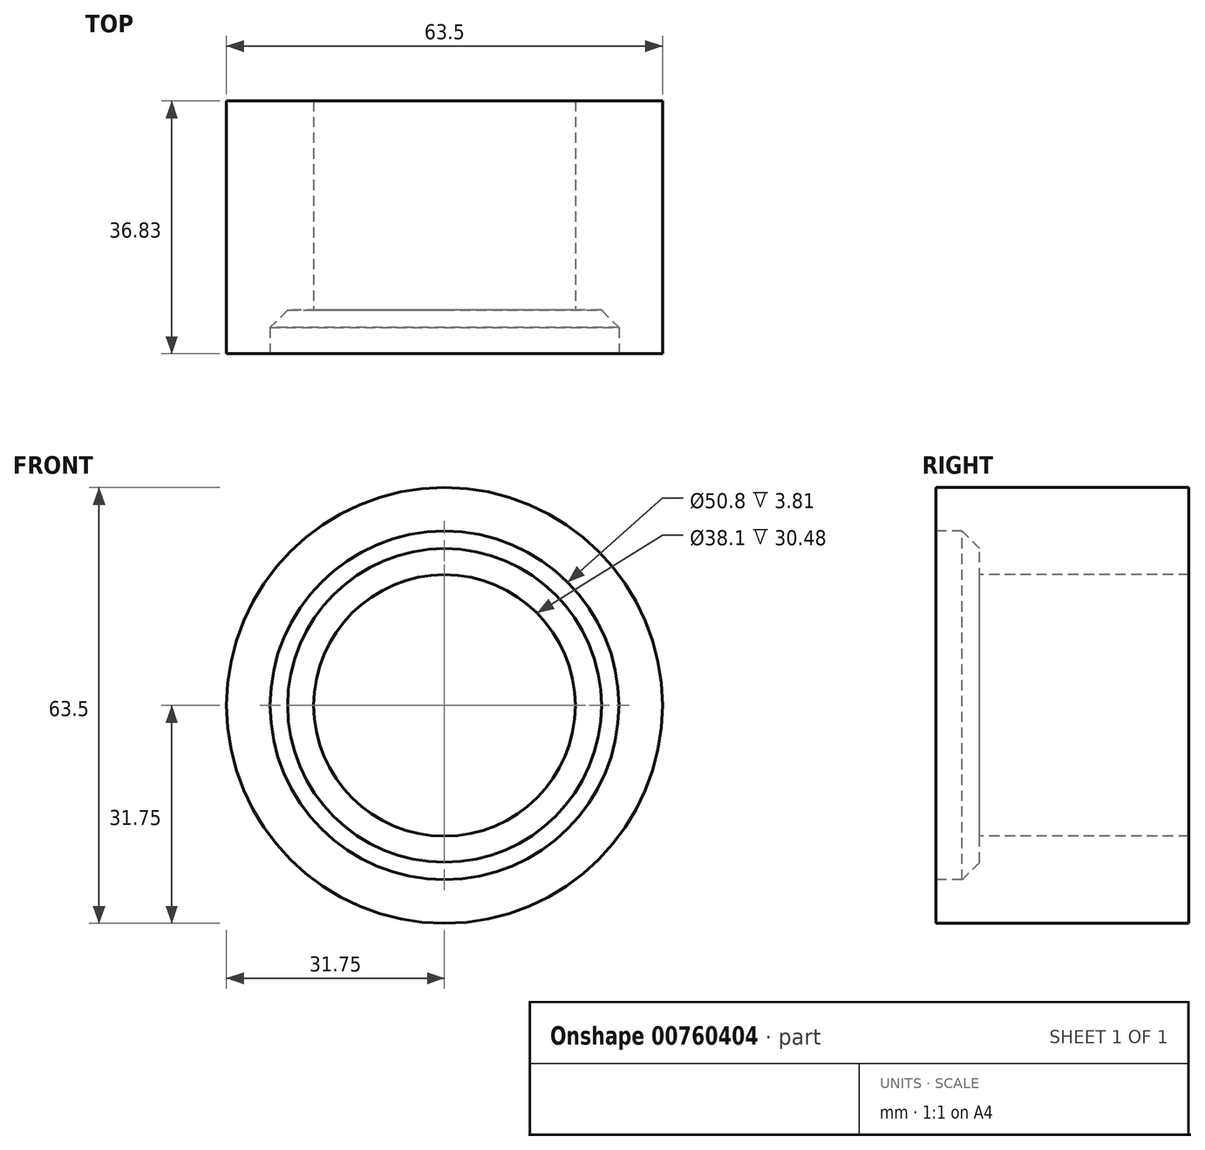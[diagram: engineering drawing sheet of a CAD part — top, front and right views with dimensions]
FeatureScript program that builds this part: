
annotation { "Feature Type Name" : "Feature", "Feature Type Description" : "" }
export const myFeature = defineFeature(function(context is Context, id is Id, definition is map)
    precondition{}
    {
        {
            var Q0;
            Q0=qCreatedBy(makeId("Front.planeOp"),FACE);
            var sketch = newSketch(context, id + "F0", { "sketchPlane" : qUnion([Q0])});
            skCircle(sketch, "E0", {"center": v(0, 0) * mm, "radius": 31.75 * mm});
            skSolve(sketch);
        }
        {
            var Q0;
            Q0 = qSketchRegion(id + "F0", true);
            extrude(context, id + "F1", {"entities" : qUnion([Q0]), "depth" : 36.83 * mm, "offsetDistance" : 25.4 * mm});
        }
        {
            var Q0;
            Q0=makeQuery(id+"F1.opExtrude","CAP_FACE",FACE,{"disambiguationData":[OSD([sQuery(id+"F0.wireOp",EDGE,"E0")])],"isStart":false});
            var sketch = newSketch(context, id + "F2", { "sketchPlane" : qUnion([Q0])});
            skCircle(sketch, "E1", {"center": v(0, 0) * mm, "radius": 25.4 * mm});
            skSolve(sketch);
        }
        {
            var Q0;
            Q0 = qSketchRegion(id + "F2", true);
            extrude(context, id + "F3", {"entities" : qUnion([Q0]), "operationType" : NewBodyOperationType.REMOVE, "oppositeDirection" : true, "depth" : 6.35 * mm, "offsetDistance" : 25.4 * mm});
        }
        {
            var Q0;
            Q0=makeQuery(id+"F3.boolean.opBoolean","COPY",EDGE,{"derivedFrom":makeQuery(id+"F3.opExtrude","CAP_EDGE",EDGE,{"disambiguationData":[OSD([sQuery(id+"F2.wireOp",EDGE,"E1")])],"isStart":false})});
            chamfer(context, id + "F4", {"entities" : qUnion([Q0]), "width" : 2.54 * mm, "tangentPropagation" : true});
        }
        {
            var Q0;
            Q0=makeQuery(id+"F3.boolean.opBoolean","COPY",FACE,{"derivedFrom":makeQuery(id+"F3.opExtrude","CAP_FACE",FACE,{"disambiguationData":[OSD([sQuery(id+"F2.wireOp",EDGE,"E1")])],"isStart":false})});
            var sketch = newSketch(context, id + "F5", { "sketchPlane" : qUnion([Q0])});
            skCircle(sketch, "E2", {"center": v(0, 0) * mm, "radius": 19.05 * mm});
            skSolve(sketch);
        }
        {
            var Q0;
            Q0 = qSketchRegion(id + "F5", true);
            extrude(context, id + "F6", {"entities" : qUnion([Q0]), "operationType" : NewBodyOperationType.REMOVE, "endBound" : BoundingType.THROUGH_ALL, "oppositeDirection" : true, "depth" : 25.4 * mm, "offsetDistance" : 25.4 * mm});
        }
    });
